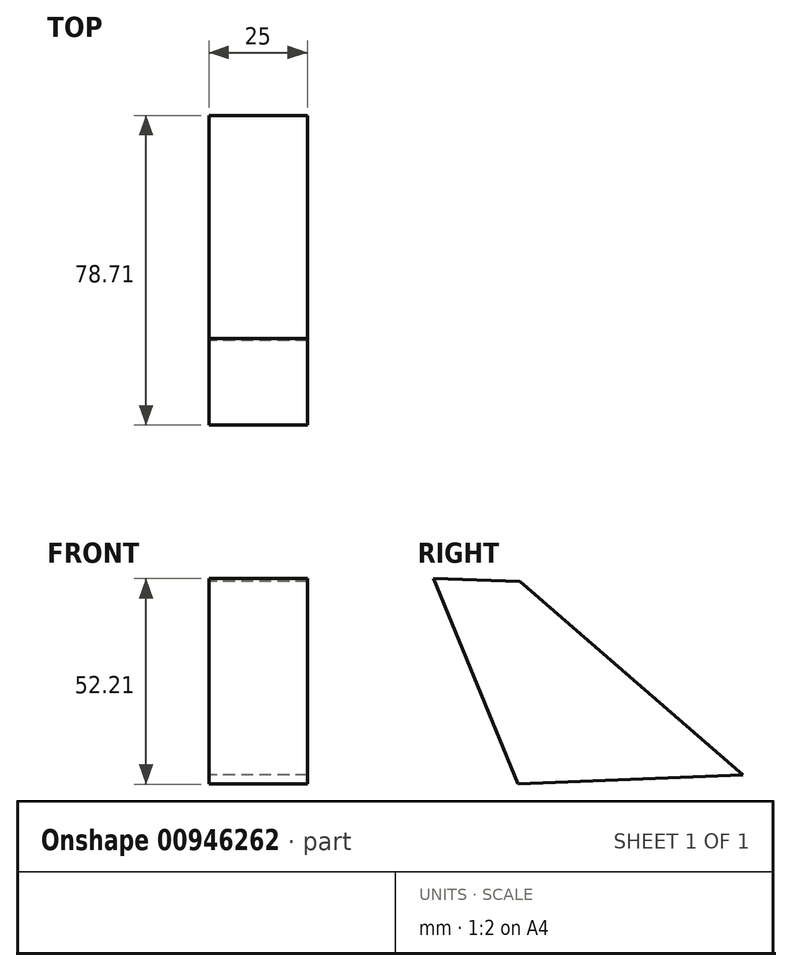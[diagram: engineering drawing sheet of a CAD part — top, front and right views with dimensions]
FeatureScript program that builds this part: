
annotation { "Feature Type Name" : "Feature", "Feature Type Description" : "" }
export const myFeature = defineFeature(function(context is Context, id is Id, definition is map)
    precondition{}
    {
        {
            var Q0;
            Q0=qCreatedBy(makeId("Right.planeOp"),FACE);
            var sketch = newSketch(context, id + "F0", { "sketchPlane" : qUnion([Q0])});
            skLineSegment(sketch, "E0.bottom", {"start": v(89.32, 61.25) * mm, "end": v(14.19, 61.25) * mm});
            skLineSegment(sketch, "E0.top", {"start": v(89.32, 29.94) * mm, "end": v(14.19, 29.94) * mm});
            skLineSegment(sketch, "E0.left", {"start": v(89.32, 61.25) * mm, "end": v(89.32, 29.94) * mm});
            skLineSegment(sketch, "E0.right", {"start": v(14.19, 61.25) * mm, "end": v(14.19, 29.94) * mm});
            skLineSegment(sketch, "E1.bottom", {"start": v(89.32, 29.94) * mm, "end": v(71.56, 29.94) * mm});
            skLineSegment(sketch, "E1.top", {"start": v(89.32, -30.2) * mm, "end": v(71.56, -30.2) * mm});
            skLineSegment(sketch, "E1.left", {"start": v(89.32, 29.94) * mm, "end": v(89.32, -30.2) * mm});
            skLineSegment(sketch, "E1.right", {"start": v(71.56, 29.94) * mm, "end": v(71.56, -30.2) * mm});
            skLineSegment(sketch, "E2.bottom", {"start": v(71.56, 29.94) * mm, "end": v(48.43, 29.94) * mm});
            skLineSegment(sketch, "E2.top", {"start": v(71.56, -12.8) * mm, "end": v(48.43, -12.8) * mm});
            skLineSegment(sketch, "E2.left", {"start": v(71.56, 29.94) * mm, "end": v(71.56, -12.8) * mm});
            skLineSegment(sketch, "E2.right", {"start": v(48.43, 29.94) * mm, "end": v(48.43, -12.8) * mm});
            skLineSegment(sketch, "E3", {"start": v(-23.31, 23.12) * mm, "end": v(33.38, -25.98) * mm});
            skLineSegment(sketch, "E4", {"start": v(33.38, -25.98) * mm, "end": v(-23.86, -28.38) * mm});
            skLineSegment(sketch, "E5", {"start": v(-23.86, -28.38) * mm, "end": v(-45.33, 23.83) * mm});
            skLineSegment(sketch, "E6", {"start": v(-45.33, 23.83) * mm, "end": v(-23.31, 23.12) * mm});
            skSolve(sketch);
        }
        {
            var Q0;
            {var subQ4=sQuery(id+"F0.wireOp",EDGE,"E2.top");Q0=makeQuery(id+"F0.imprint","IMPRINT",FACE,{"disambiguationData":[TD([[makeQuery(id+"F0.imprint","IMPRINT",EDGE,{"derivedFrom":subQ4}),-1.0]])]});}
            extrude(context, id + "F1", {"entities" : qUnion([Q0]), "oppositeDirection" : true, "depth" : 102.62 * mm, "offsetDistance" : 25.4 * mm});
        }
        {
            var Q0;
            Q0=makeQuery(id+"F0.imprint","IMPRINT",FACE,{"disambiguationData":[TD([[makeQuery(id+"F0.imprint","IMPRINT",EDGE,{"derivedFrom":sQuery(id+"F0.wireOp",EDGE,"E0.bottom")}),1.0]])]});
            extrude(context, id + "F2", {"entities" : qUnion([Q0]), "oppositeDirection" : true, "depth" : 51.82 * mm, "offsetDistance" : 25.4 * mm});
        }
        {
            var Q0;
            {var subQ1=sQuery(id+"F0.wireOp",EDGE,"E1.top");Q0=makeQuery(id+"F0.imprint","IMPRINT",FACE,{"disambiguationData":[TD([[makeQuery(id+"F0.imprint","IMPRINT",EDGE,{"derivedFrom":subQ1}),-1.0]])]});}
            extrude(context, id + "F3", {"entities" : qUnion([Q0]), "depth" : 45.72 * mm, "offsetDistance" : 25.4 * mm});
        }
        {
            var Q0;
            Q0=makeQuery(id+"F2.opExtrude","SWEPT_EDGE",EDGE,{"disambiguationData":[OSD([sQuery(id+"F0.wireOp",EDGE,"E0.bottom"),sQuery(id+"F0.wireOp",EDGE,"E0.right")])]});
            var Q1;
            Q1=makeQuery(id+"F1.opExtrude","SWEPT_EDGE",EDGE,{"disambiguationData":[OSD([sQuery(id+"F0.wireOp",EDGE,"E0.top"),sQuery(id+"F0.wireOp",EDGE,"E2.right")])]});
            chamfer(context, id + "F4", {"entities" : qUnion([Q0, Q1]), "width" : 5.08 * mm, "tangentPropagation" : true});
        }
        {
            var Q0;
            Q0=makeQuery(id+"F1.opExtrude","SWEPT_EDGE",EDGE,{"disambiguationData":[OSD([sQuery(id+"F0.wireOp",EDGE,"E0.top"),sQuery(id+"F0.wireOp",EDGE,"E1.right")])]});
            fillet(context, id + "F5", {"entities" : qUnion([Q0]), "radius" : 19.62 * mm, "tangentPropagation" : true, "allowEdgeOverflow" : false});
        }
        {
            var Q0;
            Q0=makeQuery(id+"F0.imprint","IMPRINT",FACE,{"disambiguationData":[TD([[makeQuery(id+"F0.imprint","IMPRINT",EDGE,{"derivedFrom":sQuery(id+"F0.wireOp",EDGE,"E3")}),-1.0]])]});
            extrude(context, id + "F6", {"entities" : qUnion([Q0]), "operationType" : NewBodyOperationType.INTERSECT, "endBound" : BoundingType.SYMMETRIC, "oppositeDirection" : true, "depth" : 25 * mm, "offsetDistance" : 25 * mm});
        }
        {
            var Q0;
            Q0=makeQuery(id+"F0.imprint","IMPRINT",FACE,{"disambiguationData":[TD([[makeQuery(id+"F0.imprint","IMPRINT",EDGE,{"derivedFrom":sQuery(id+"F0.wireOp",EDGE,"E3")}),-1.0]])]});
            extrude(context, id + "F7", {"entities" : qUnion([Q0]), "endBound" : BoundingType.SYMMETRIC, "depth" : 25 * mm, "offsetDistance" : 25 * mm});
        }
    });
